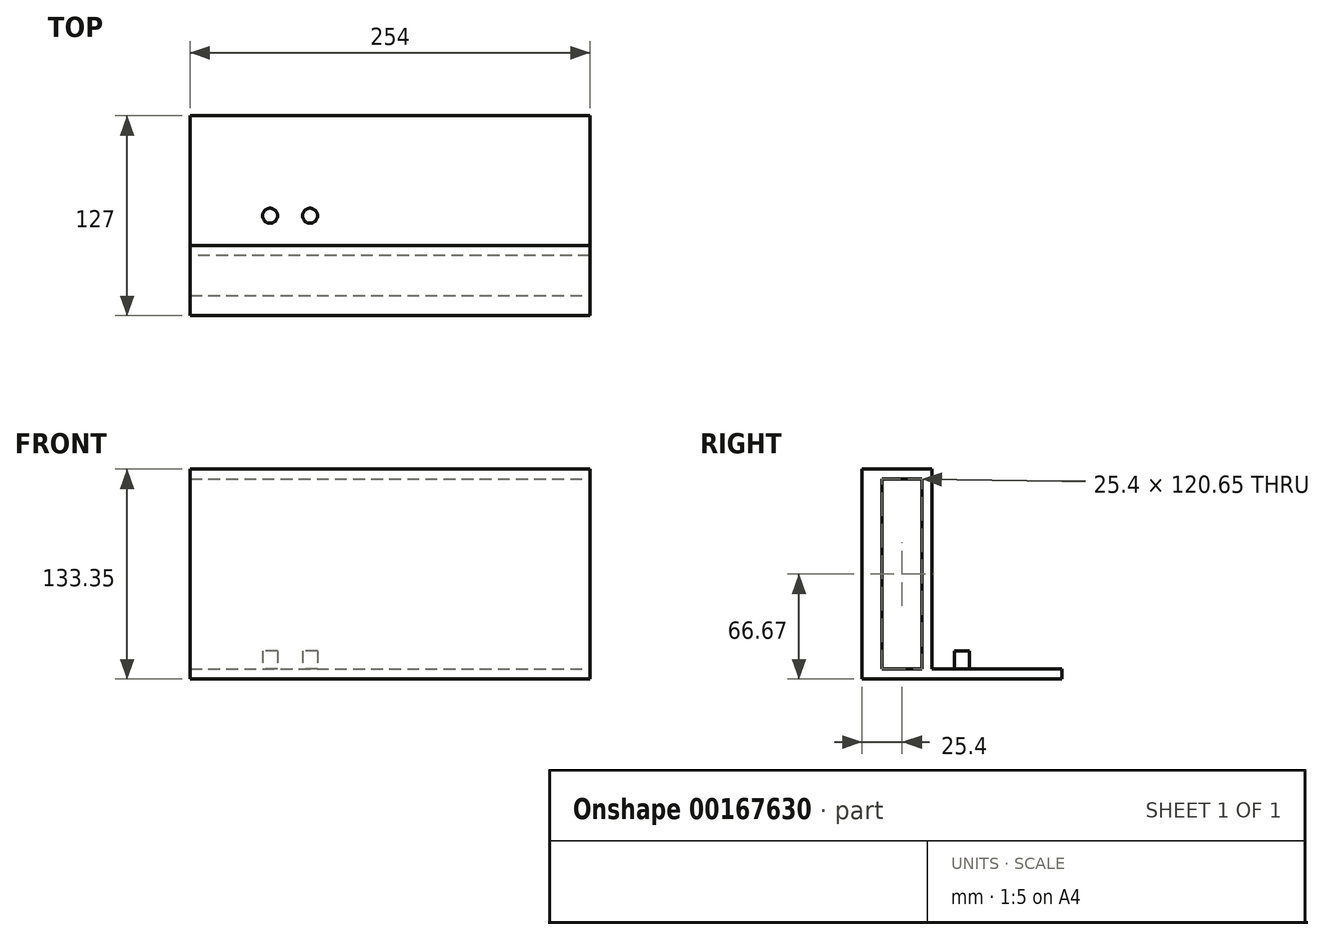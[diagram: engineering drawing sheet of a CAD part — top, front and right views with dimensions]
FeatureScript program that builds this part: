
annotation { "Feature Type Name" : "Feature", "Feature Type Description" : "" }
export const myFeature = defineFeature(function(context is Context, id is Id, definition is map)
    precondition{}
    {
        {
            var Q0;
            Q0=qCreatedBy(makeId("Top.planeOp"),FACE);
            var sketch = newSketch(context, id + "F0", { "sketchPlane" : qUnion([Q0])});
            skLineSegment(sketch, "E0.bottom", {"start": v(-63.5, 63.5) * mm, "end": v(63.5, 63.5) * mm});
            skLineSegment(sketch, "E0.top", {"start": v(-63.5, -63.5) * mm, "end": v(63.5, -63.5) * mm});
            skLineSegment(sketch, "E0.left", {"start": v(-63.5, 63.5) * mm, "end": v(-63.5, -63.5) * mm});
            skLineSegment(sketch, "E0.right", {"start": v(63.5, 63.5) * mm, "end": v(63.5, -63.5) * mm});
            skPoint(sketch, "E1", {"position": v(0, 63.5) * mm});
            skPoint(sketch, "E2", {"position": v(63.5, 0) * mm});
            skSolve(sketch);
        }
        {
            var Q0;
            Q0 = qSketchRegion(id + "F0", true);
            extrude(context, id + "F1", {"entities" : qUnion([Q0]), "endBound" : BoundingType.SYMMETRIC, "depth" : 6.35 * mm});
        }
        {
            var Q0;
            Q0=makeQuery(id+"F1.opExtrude","CAP_FACE",FACE,{"disambiguationData":[OSD([sQuery(id+"F0.wireOp",EDGE,"E0.bottom"),sQuery(id+"F0.wireOp",EDGE,"E0.top"),sQuery(id+"F0.wireOp",EDGE,"E0.left"),sQuery(id+"F0.wireOp",EDGE,"E0.right")])],"isStart":false});
            var sketch = newSketch(context, id + "F2", { "sketchPlane" : qUnion([Q0])});
            skLineSegment(sketch, "E3", {"start": v(-12.7, 0) * mm, "end": v(12.7, 0) * mm, "construction": true});
            skPoint(sketch, "E4", {"position": v(0, 0) * mm});
            skCircle(sketch, "E5", {"center": v(-12.7, 0) * mm, "radius": 4.76 * mm});
            skCircle(sketch, "E6", {"center": v(12.7, 0) * mm, "radius": 4.76 * mm});
            skSolve(sketch);
        }
        {
            var Q0;
            Q0=makeQuery(id+"F2.imprint","IMPRINT",FACE,{"disambiguationData":[TD([[makeQuery(id+"F2.imprint","IMPRINT",EDGE,{"derivedFrom":sQuery(id+"F2.wireOp",EDGE,"E5")}),1.0]])]});
            var Q1;
            Q1=makeQuery(id+"F2.imprint","IMPRINT",FACE,{"disambiguationData":[TD([[makeQuery(id+"F2.imprint","IMPRINT",EDGE,{"derivedFrom":sQuery(id+"F2.wireOp",EDGE,"E6")}),1.0]])]});
            extrude(context, id + "F3", {"entities" : qUnion([Q0, Q1]), "operationType" : NewBodyOperationType.ADD, "depth" : 11.43 * mm});
        }
        {
            var Q0;
            Q0=makeQuery(id+"F1.opExtrude","CAP_FACE",FACE,{"disambiguationData":[OSD([sQuery(id+"F0.wireOp",EDGE,"E0.bottom"),sQuery(id+"F0.wireOp",EDGE,"E0.top"),sQuery(id+"F0.wireOp",EDGE,"E0.left"),sQuery(id+"F0.wireOp",EDGE,"E0.right")])],"isStart":false});
            var sketch = newSketch(context, id + "F4", { "sketchPlane" : qUnion([Q0])});
            skLineSegment(sketch, "E7.bottom", {"start": v(-63.5, -63.5) * mm, "end": v(63.5, -63.5) * mm});
            skLineSegment(sketch, "E7.top", {"start": v(-63.5, -50.8) * mm, "end": v(63.5, -50.8) * mm});
            skLineSegment(sketch, "E7.left", {"start": v(-63.5, -63.5) * mm, "end": v(-63.5, -50.8) * mm});
            skLineSegment(sketch, "E7.right", {"start": v(63.5, -63.5) * mm, "end": v(63.5, -50.8) * mm});
            skSolve(sketch);
        }
        {
            var Q0;
            Q0 = qSketchRegion(id + "F4", true);
            extrude(context, id + "F5", {"entities" : qUnion([Q0]), "operationType" : NewBodyOperationType.ADD, "depth" : 127 * mm});
        }
        {
            var Q0;
            Q0=makeQuery(id+"F1.opExtrude","CAP_FACE",FACE,{"disambiguationData":[OSD([sQuery(id+"F0.wireOp",EDGE,"E0.bottom"),sQuery(id+"F0.wireOp",EDGE,"E0.top"),sQuery(id+"F0.wireOp",EDGE,"E0.left"),sQuery(id+"F0.wireOp",EDGE,"E0.right")])],"isStart":false});
            var sketch = newSketch(context, id + "F6", { "sketchPlane" : qUnion([Q0])});
            skLineSegment(sketch, "E8", {"start": v(63.5, -50.8) * mm, "end": v(63.5, -19.05) * mm, "construction": true});
            skLineSegment(sketch, "E9", {"start": v(63.5, -19.05) * mm, "end": v(-63.5, -19.05) * mm});
            skLineSegment(sketch, "E10.0", {"start": v(63.5, -25.4) * mm, "end": v(-63.5, -25.4) * mm});
            skLineSegment(sketch, "E11", {"start": v(-63.5, -25.4) * mm, "end": v(-63.5, -19.05) * mm});
            skSolve(sketch);
        }
        {
            var Q0;
            {var subQ0=sQuery(id+"F6.wireOp",EDGE,"E9");Q0=makeQuery(id+"F6.imprint","IMPRINT",FACE,{"disambiguationData":[TD([[makeQuery(id+"F6.imprint","IMPRINT",EDGE,{"derivedFrom":subQ0}),1.0]])]});}
            var Q1;
            Q1=makeQuery(id+"F5.opExtrude","CAP_FACE",FACE,{"disambiguationData":[OSD([sQuery(id+"F4.wireOp",EDGE,"E7.bottom"),sQuery(id+"F4.wireOp",EDGE,"E7.top"),sQuery(id+"F4.wireOp",EDGE,"E7.left"),sQuery(id+"F4.wireOp",EDGE,"E7.right")])],"isStart":false});
            extrude(context, id + "F7", {"entities" : qUnion([Q0]), "operationType" : NewBodyOperationType.ADD, "endBound" : BoundingType.UP_TO_SURFACE, "endBoundEntityFace" : qUnion([Q1]), "depth" : 25.4 * mm});
        }
        {
            var Q0;
            {var subQ0=sQuery(id+"F0.wireOp",EDGE,"E0.right");var subQ1=sQuery(id+"F4.wireOp",EDGE,"E7.right");Q0=makeQuery(id+"F7.boolean.opBoolean","MERGE",FACE,{"derivedFrom":[makeQuery(id+"FFZJ1dubnRmx0ky_1.1.F5.boolean.opBoolean","MERGE",FACE,{"derivedFrom":[makeQuery(id+"F5.boolean.opBoolean","MERGE",FACE,{"derivedFrom":[makeQuery(id+"F1.opExtrude","SWEPT_FACE",FACE,{"disambiguationData":[OSD([subQ0])]}),makeQuery(id+"F5.opExtrude","SWEPT_FACE",FACE,{"disambiguationData":[OSD([subQ1])]})]}),makeQuery(id+"FFZJ1dubnRmx0ky_1.1.F5.opExtrude","SWEPT_FACE",FACE,{"disambiguationData":[OSD([subQ1])]})]}),makeQuery(id+"F7.opExtrude","SWEPT_FACE",FACE,{"disambiguationData":[OSD([subQ0])]})]});}
            extrude(context, id + "F8", {"entities" : qUnion([Q0]), "operationType" : NewBodyOperationType.ADD, "depth" : 127 * mm});
        }
        {
            var Q0;
            {var subQ0=sQuery(id+"F6.wireOp",EDGE,"E9");Q0=makeQuery(id+"F8.boolean.opBoolean","MERGE",FACE,{"derivedFrom":[makeQuery(id+"F7.opExtrude","SWEPT_FACE",FACE,{"disambiguationData":[OSD([subQ0])]}),makeQuery(id+"F8.opExtrude","SWEPT_FACE",FACE,{"disambiguationData":[OSD([sQuery(id+"F0.wireOp",EDGE,"E0.right"),subQ0])]})]});}
            var sketch = newSketch(context, id + "F9", { "sketchPlane" : qUnion([Q0])});
            skLineSegment(sketch, "E12.bottom", {"start": v(-190.5, 130.18) * mm, "end": v(63.5, 130.18) * mm});
            skLineSegment(sketch, "E12.top", {"start": v(-190.5, 123.83) * mm, "end": v(63.5, 123.83) * mm});
            skLineSegment(sketch, "E12.left", {"start": v(-190.5, 130.18) * mm, "end": v(-190.5, 123.83) * mm});
            skLineSegment(sketch, "E12.right", {"start": v(63.5, 130.18) * mm, "end": v(63.5, 123.83) * mm});
            skSolve(sketch);
        }
        {
            var Q0;
            Q0 = qSketchRegion(id + "F9", true);
            var Q1;
            {var subQ0=sQuery(id+"F4.wireOp",EDGE,"E7.right");var subQ1=sQuery(id+"F4.wireOp",EDGE,"E7.top");var subQ2=sQuery(id+"F0.wireOp",EDGE,"E0.right");Q1=makeQuery(id+"F8.boolean.opBoolean","MERGE",FACE,{"derivedFrom":[makeQuery(id+"F5.opExtrude","SWEPT_FACE",FACE,{"disambiguationData":[OSD([subQ1])]}),makeQuery(id+"F8.opExtrude","SWEPT_FACE",FACE,{"disambiguationData":[OSD([subQ2,subQ1,subQ0]),TDD([makeQuery(id+"F5.opExtrude","SWEPT_EDGE",EDGE,{"disambiguationData":[OSD([subQ2,subQ1,subQ0])]})])]})]});}
            extrude(context, id + "F10", {"entities" : qUnion([Q0]), "operationType" : NewBodyOperationType.ADD, "endBound" : BoundingType.UP_TO_SURFACE, "oppositeDirection" : true, "endBoundEntityFace" : qUnion([Q1]), "depth" : 25.4 * mm});
        }
    });
